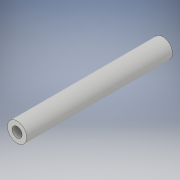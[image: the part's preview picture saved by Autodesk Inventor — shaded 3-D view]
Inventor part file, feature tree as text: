
AUTODESK INVENTOR PART (.ipt)
format: ipt  version: 2017 (Build 210142000, 142)  size: 90,624 bytes
history: native  units: in
note: dims shown in document units (in); Inventor stores cm internally (conversion verified against a paired STEP export)
features: extrude x1, sketch x1
ambient origin geometry x8: Origin, YZ Plane, XZ Plane, XY Plane, X Axis, Y Axis, Z Axis, Center Point
bodies: Solid1 (feature_tree)
feature tree (2):
  extrude  "Extrusion1"  [1 undecoded]
  sketch  "Sketch1"  dims[d0=3.75in d1=0.0in]
note: 1 required parameter value undecoded (feature->parameter linkage not recoverable at this tier; creation-order binding heuristic only, values carry confidence <= 0.55)
